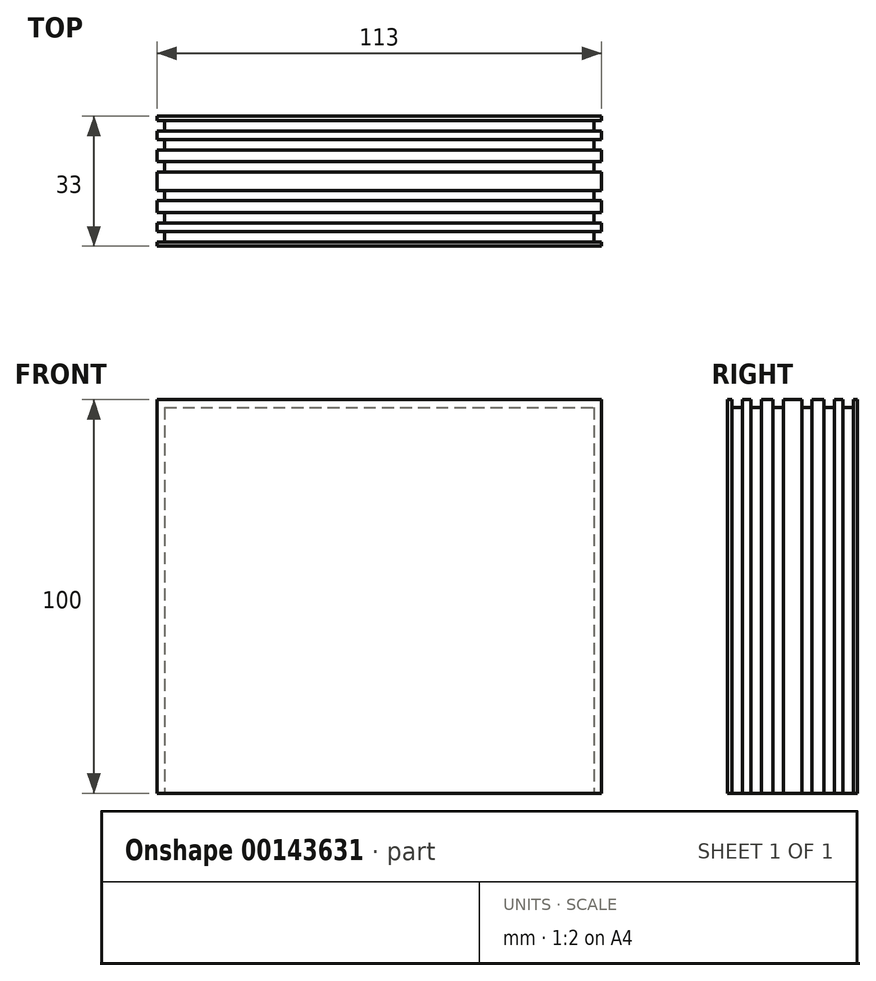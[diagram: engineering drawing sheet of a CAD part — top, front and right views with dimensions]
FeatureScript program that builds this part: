
annotation { "Feature Type Name" : "Feature", "Feature Type Description" : "" }
export const myFeature = defineFeature(function(context is Context, id is Id, definition is map)
    precondition{}
    {
        {
            var Q0;
            Q0=qCreatedBy(makeId("Front.planeOp"),FACE);
            var sketch = newSketch(context, id + "F0", { "sketchPlane" : qUnion([Q0])});
            skLineSegment(sketch, "E0.bottom", {"start": v(56.5, 50) * mm, "end": v(-56.5, 50) * mm});
            skLineSegment(sketch, "E0.top", {"start": v(56.5, -50) * mm, "end": v(-56.5, -50) * mm});
            skLineSegment(sketch, "E0.left", {"start": v(56.5, 50) * mm, "end": v(56.5, -50) * mm});
            skLineSegment(sketch, "E0.right", {"start": v(-56.5, 50) * mm, "end": v(-56.5, -50) * mm});
            skPoint(sketch, "E0.middle", {"position": v(0, 0) * mm});
            skSolve(sketch);
        }
        {
            var Q0;
            Q0 = qSketchRegion(id + "F0", true);
            extrude(context, id + "F1", {"entities" : qUnion([Q0]), "endBound" : BoundingType.SYMMETRIC, "depth" : 33 * mm});
        }
        {
            var Q0;
            Q0=makeQuery(id+"F1.opExtrude","SWEPT_FACE",FACE,{"disambiguationData":[OSD([sQuery(id+"F0.wireOp",EDGE,"E0.bottom")])]});
            var sketch = newSketch(context, id + "F2", { "sketchPlane" : qUnion([Q0])});
            skLineSegment(sketch, "E1.bottom", {"start": v(-56.5, -12.77) * mm, "end": v(56.5, -12.77) * mm});
            skLineSegment(sketch, "E1.top", {"start": v(-56.5, -15.42) * mm, "end": v(56.5, -15.42) * mm});
            skLineSegment(sketch, "E1.left", {"start": v(-56.5, -12.77) * mm, "end": v(-56.5, -15.42) * mm});
            skLineSegment(sketch, "E1.right", {"start": v(56.5, -12.77) * mm, "end": v(56.5, -15.42) * mm});
            skLineSegment(sketch, "E2", {"start": v(-56.5, 0) * mm, "end": v(56.5, 0) * mm});
            skLineSegment(sketch, "E3.MirrorCS", {"start": v(-56.5, 12.77) * mm, "end": v(56.5, 12.77) * mm});
            skLineSegment(sketch, "E4.MirrorCS", {"start": v(-56.5, 12.77) * mm, "end": v(-56.5, 15.42) * mm});
            skLineSegment(sketch, "E5.MirrorCS", {"start": v(-56.5, 15.42) * mm, "end": v(56.5, 15.42) * mm});
            skLineSegment(sketch, "E6.MirrorCS", {"start": v(56.5, 12.77) * mm, "end": v(56.5, 15.42) * mm});
            skLineSegment(sketch, "E7.bottom", {"start": v(-56.5, -7.95) * mm, "end": v(56.5, -7.95) * mm});
            skLineSegment(sketch, "E7.top", {"start": v(-56.5, -10.6) * mm, "end": v(56.5, -10.6) * mm});
            skLineSegment(sketch, "E7.left", {"start": v(-56.5, -7.95) * mm, "end": v(-56.5, -10.6) * mm});
            skLineSegment(sketch, "E7.right", {"start": v(56.5, -7.95) * mm, "end": v(56.5, -10.6) * mm});
            skLineSegment(sketch, "E8.bottom", {"start": v(-56.5, -2.32) * mm, "end": v(56.5, -2.32) * mm});
            skLineSegment(sketch, "E8.top", {"start": v(-56.5, -4.96) * mm, "end": v(56.5, -4.96) * mm});
            skLineSegment(sketch, "E8.left", {"start": v(-56.5, -2.32) * mm, "end": v(-56.5, -4.96) * mm});
            skLineSegment(sketch, "E8.right", {"start": v(56.5, -2.32) * mm, "end": v(56.5, -4.96) * mm});
            skLineSegment(sketch, "E9.MirrorCS", {"start": v(-56.5, 2.32) * mm, "end": v(56.5, 2.32) * mm});
            skLineSegment(sketch, "E10.MirrorCS", {"start": v(-56.5, 2.32) * mm, "end": v(-56.5, 4.96) * mm});
            skLineSegment(sketch, "E11.MirrorCS", {"start": v(-56.5, 4.96) * mm, "end": v(56.5, 4.96) * mm});
            skLineSegment(sketch, "E12.MirrorCS", {"start": v(56.5, 2.32) * mm, "end": v(56.5, 4.96) * mm});
            skLineSegment(sketch, "E13.MirrorCS", {"start": v(-56.5, 7.95) * mm, "end": v(56.5, 7.95) * mm});
            skLineSegment(sketch, "E14.MirrorCS", {"start": v(-56.5, 7.95) * mm, "end": v(-56.5, 10.6) * mm});
            skLineSegment(sketch, "E15.MirrorCS", {"start": v(56.5, 7.95) * mm, "end": v(56.5, 10.6) * mm});
            skLineSegment(sketch, "E16.MirrorCS", {"start": v(-56.5, 10.6) * mm, "end": v(56.5, 10.6) * mm});
            skSolve(sketch);
        }
        {
            var Q0;
            Q0 = qSketchRegion(id + "F2", true);
            extrude(context, id + "F3", {"entities" : qUnion([Q0]), "operationType" : NewBodyOperationType.REMOVE, "oppositeDirection" : true, "depth" : 2 * mm});
        }
        {
            var Q0;
            Q0=makeQuery(id+"F1.opExtrude","SWEPT_FACE",FACE,{"disambiguationData":[OSD([sQuery(id+"F0.wireOp",EDGE,"E0.left")])]});
            var sketch = newSketch(context, id + "F4", { "sketchPlane" : qUnion([Q0])});
            skLineSegment(sketch, "E17.bottom", {"start": v(12.77, 48) * mm, "end": v(15.42, 48) * mm});
            skLineSegment(sketch, "E17.top", {"start": v(12.77, -50) * mm, "end": v(15.42, -50) * mm});
            skLineSegment(sketch, "E17.left", {"start": v(12.77, 48) * mm, "end": v(12.77, -50) * mm});
            skLineSegment(sketch, "E17.right", {"start": v(15.42, 48) * mm, "end": v(15.42, -50) * mm});
            skLineSegment(sketch, "E18.bottom", {"start": v(7.95, 48) * mm, "end": v(10.6, 48) * mm});
            skLineSegment(sketch, "E18.top", {"start": v(7.95, -50) * mm, "end": v(10.6, -50) * mm});
            skLineSegment(sketch, "E18.left", {"start": v(7.95, 48) * mm, "end": v(7.95, -50) * mm});
            skLineSegment(sketch, "E18.right", {"start": v(10.6, 48) * mm, "end": v(10.6, -50) * mm});
            skLineSegment(sketch, "E19.bottom", {"start": v(2.32, 48) * mm, "end": v(4.96, 48) * mm});
            skLineSegment(sketch, "E19.top", {"start": v(2.32, -50) * mm, "end": v(4.96, -50) * mm});
            skLineSegment(sketch, "E19.left", {"start": v(2.32, 48) * mm, "end": v(2.32, -50) * mm});
            skLineSegment(sketch, "E19.right", {"start": v(4.96, 48) * mm, "end": v(4.96, -50) * mm});
            skLineSegment(sketch, "E20", {"start": v(0, 50) * mm, "end": v(0, -50) * mm});
            skLineSegment(sketch, "E21.MirrorCS", {"start": v(-2.32, 48) * mm, "end": v(-4.96, 48) * mm});
            skLineSegment(sketch, "E22.MirrorCS", {"start": v(-4.96, 48) * mm, "end": v(-4.96, -50) * mm});
            skLineSegment(sketch, "E23.MirrorCS", {"start": v(-2.32, 48) * mm, "end": v(-2.32, -50) * mm});
            skLineSegment(sketch, "E24.MirrorCS", {"start": v(-2.32, -50) * mm, "end": v(-4.96, -50) * mm});
            skLineSegment(sketch, "E25.MirrorCS", {"start": v(-7.95, -50) * mm, "end": v(-10.6, -50) * mm});
            skLineSegment(sketch, "E26.MirrorCS", {"start": v(-7.95, 48) * mm, "end": v(-7.95, -50) * mm});
            skLineSegment(sketch, "E27.MirrorCS", {"start": v(-10.6, 48) * mm, "end": v(-10.6, -50) * mm});
            skLineSegment(sketch, "E28.MirrorCS", {"start": v(-7.95, 48) * mm, "end": v(-10.6, 48) * mm});
            skLineSegment(sketch, "E29.MirrorCS", {"start": v(-12.77, 48) * mm, "end": v(-12.77, -50) * mm});
            skLineSegment(sketch, "E30.MirrorCS", {"start": v(-12.77, 48) * mm, "end": v(-15.42, 48) * mm});
            skLineSegment(sketch, "E31.MirrorCS", {"start": v(-15.42, 48) * mm, "end": v(-15.42, -50) * mm});
            skLineSegment(sketch, "E32.MirrorCS", {"start": v(-12.77, -50) * mm, "end": v(-15.42, -50) * mm});
            skSolve(sketch);
        }
        {
            var Q0;
            Q0 = qSketchRegion(id + "F4", true);
            extrude(context, id + "F5", {"entities" : qUnion([Q0]), "operationType" : NewBodyOperationType.REMOVE, "oppositeDirection" : true, "depth" : 2 * mm});
        }
        {
            var Q0;
            Q0=makeQuery(id+"F1.opExtrude","SWEPT_FACE",FACE,{"disambiguationData":[OSD([sQuery(id+"F0.wireOp",EDGE,"E0.right")])]});
            var sketch = newSketch(context, id + "F6", { "sketchPlane" : qUnion([Q0])});
            skLineSegment(sketch, "E33.bottom", {"start": v(-15.42, 48) * mm, "end": v(-12.77, 48) * mm});
            skLineSegment(sketch, "E33.top", {"start": v(-15.42, -50) * mm, "end": v(-12.77, -50) * mm});
            skLineSegment(sketch, "E33.left", {"start": v(-15.42, 48) * mm, "end": v(-15.42, -50) * mm});
            skLineSegment(sketch, "E33.right", {"start": v(-12.77, 48) * mm, "end": v(-12.77, -50) * mm});
            skLineSegment(sketch, "E34.bottom", {"start": v(-10.6, 48) * mm, "end": v(-7.95, 48) * mm});
            skLineSegment(sketch, "E34.top", {"start": v(-10.6, -50) * mm, "end": v(-7.95, -50) * mm});
            skLineSegment(sketch, "E34.left", {"start": v(-10.6, 48) * mm, "end": v(-10.6, -50) * mm});
            skLineSegment(sketch, "E34.right", {"start": v(-7.95, 48) * mm, "end": v(-7.95, -50) * mm});
            skLineSegment(sketch, "E35.bottom", {"start": v(-4.96, 48) * mm, "end": v(-2.32, 48) * mm});
            skLineSegment(sketch, "E35.top", {"start": v(-4.96, -50) * mm, "end": v(-2.32, -50) * mm});
            skLineSegment(sketch, "E35.left", {"start": v(-4.96, 48) * mm, "end": v(-4.96, -50) * mm});
            skLineSegment(sketch, "E35.right", {"start": v(-2.32, 48) * mm, "end": v(-2.32, -50) * mm});
            skLineSegment(sketch, "E36", {"start": v(0, 50) * mm, "end": v(0, -50) * mm});
            skLineSegment(sketch, "E37.MirrorCS", {"start": v(2.32, 48) * mm, "end": v(2.32, -50) * mm});
            skLineSegment(sketch, "E38.MirrorCS", {"start": v(4.96, 48) * mm, "end": v(4.96, -50) * mm});
            skLineSegment(sketch, "E39.MirrorCS", {"start": v(7.95, 48) * mm, "end": v(7.95, -50) * mm});
            skLineSegment(sketch, "E40.MirrorCS", {"start": v(10.6, 48) * mm, "end": v(10.6, -50) * mm});
            skLineSegment(sketch, "E41.MirrorCS", {"start": v(12.77, 48) * mm, "end": v(12.77, -50) * mm});
            skLineSegment(sketch, "E42.MirrorCS", {"start": v(15.42, 48) * mm, "end": v(15.42, -50) * mm});
            skLineSegment(sketch, "E43.MirrorCS", {"start": v(10.6, 48) * mm, "end": v(7.95, 48) * mm});
            skLineSegment(sketch, "E44.MirrorCS", {"start": v(4.96, 48) * mm, "end": v(2.32, 48) * mm});
            skLineSegment(sketch, "E45.MirrorCS", {"start": v(4.96, -50) * mm, "end": v(2.32, -50) * mm});
            skLineSegment(sketch, "E46.MirrorCS", {"start": v(10.6, -50) * mm, "end": v(7.95, -50) * mm});
            skLineSegment(sketch, "E47.MirrorCS", {"start": v(15.42, -50) * mm, "end": v(12.77, -50) * mm});
            skLineSegment(sketch, "E48.MirrorCS", {"start": v(15.42, 48) * mm, "end": v(12.77, 48) * mm});
            skSolve(sketch);
        }
        {
            var Q0;
            Q0 = qSketchRegion(id + "F6", true);
            extrude(context, id + "F7", {"entities" : qUnion([Q0]), "operationType" : NewBodyOperationType.REMOVE, "oppositeDirection" : true, "depth" : 2 * mm});
        }
    });
